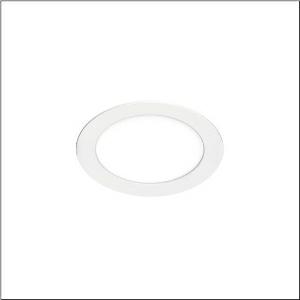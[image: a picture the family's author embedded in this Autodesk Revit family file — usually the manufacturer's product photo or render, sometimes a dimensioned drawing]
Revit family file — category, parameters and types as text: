
# Revit family: lunis_41_flat_51dr10mfhcb
name_source: partatom
category: Lighting Fixtures
units: mm (PartAtom-declared; Revit-internal decimal feet)

## family parameters
Cut with Voids When Loaded = No
Host = Face
Light Source = No
Part Type = Normal
Room Calculation Point = No
Round Connector Dimension = Use Diameter
Shared = No

## types (1)
- --- (1 x LED, 2500 lm, 19.5 W, 6500K)
    Apparent Load = 20 VA
    CIE Flux Codes = 49 80 96 100 100
    Color Rendering = 80
    Color Temperature = 6500K
    Default Elevation = 1800 mm
    Description = Lunis 41,  Flat, downlight, light emission: direct distribution, LED rated luminous flux: 2.430lm, light colour: 840/865, mains connection: 230V, AC, 50/60Hz, housing, round, of aluminium, coated, traffic white (RAL 9016), diameter: 225mm, protection rating (complete): IP20, protection rating (on room side): IP44, insulation class (complete): insulation class II (safety insulation), certification: CE, permissible ambient temperature for indoor applications: -20..+40°C, packaging unit: 1 piece
    Height = 0 mm  [stored 0 ft]
    Lamp = 1 x LED
    Lamp Light Flux = 2500 lm
    Lamp Power = 19.5 W
    Lamp count = 1
    Length = 225 mm
    Luminous efficacy = 128 lm/W
    Manufacturer = Siteco
    ModVariant = No
    Model = 51DR10MFHCB
    Mounting Place = Ceiling
    Mounting Type = Recessed
    Number of Poles = 1
    OnlyDefault = Yes
    Power Factor = 1
    Product Name = Lunis 41 Flat
    Product group = downlight
    ProductGroupID = 400
    Protection Class = Protection class II
    Protection Degree = IP 20
    RLX_Detail_Level = 1
    RLX_Emergency_Light_Flux = 0 lm
    RLX_Emergency_Type = 0
    RLX_Emergency_Type_DB = No
    RlxData = <blob elided: 11589 chars, md5=23212249>
    Socket = socket
    Standby Power = 0 W
    System Light Flux = 2500 lm
    System Power = 20 W
    Type Comments = individual setting: colour temperature 6500K
    Type Image = l_1340923.jpg
    URL = http://relux.com
    VarID = @adj_001615
    Voltage = 0 V
    Weight = 0.00 kg
    Width = 0 mm  [stored 0 ft]

note: [stored X ft] marks values corroborated as IEEE doubles in the binary element streams (Revit-internal decimal feet)

## geometry (parser evidence)
native form markers: Sweep x10
no freeform markers — native parametric forms only
